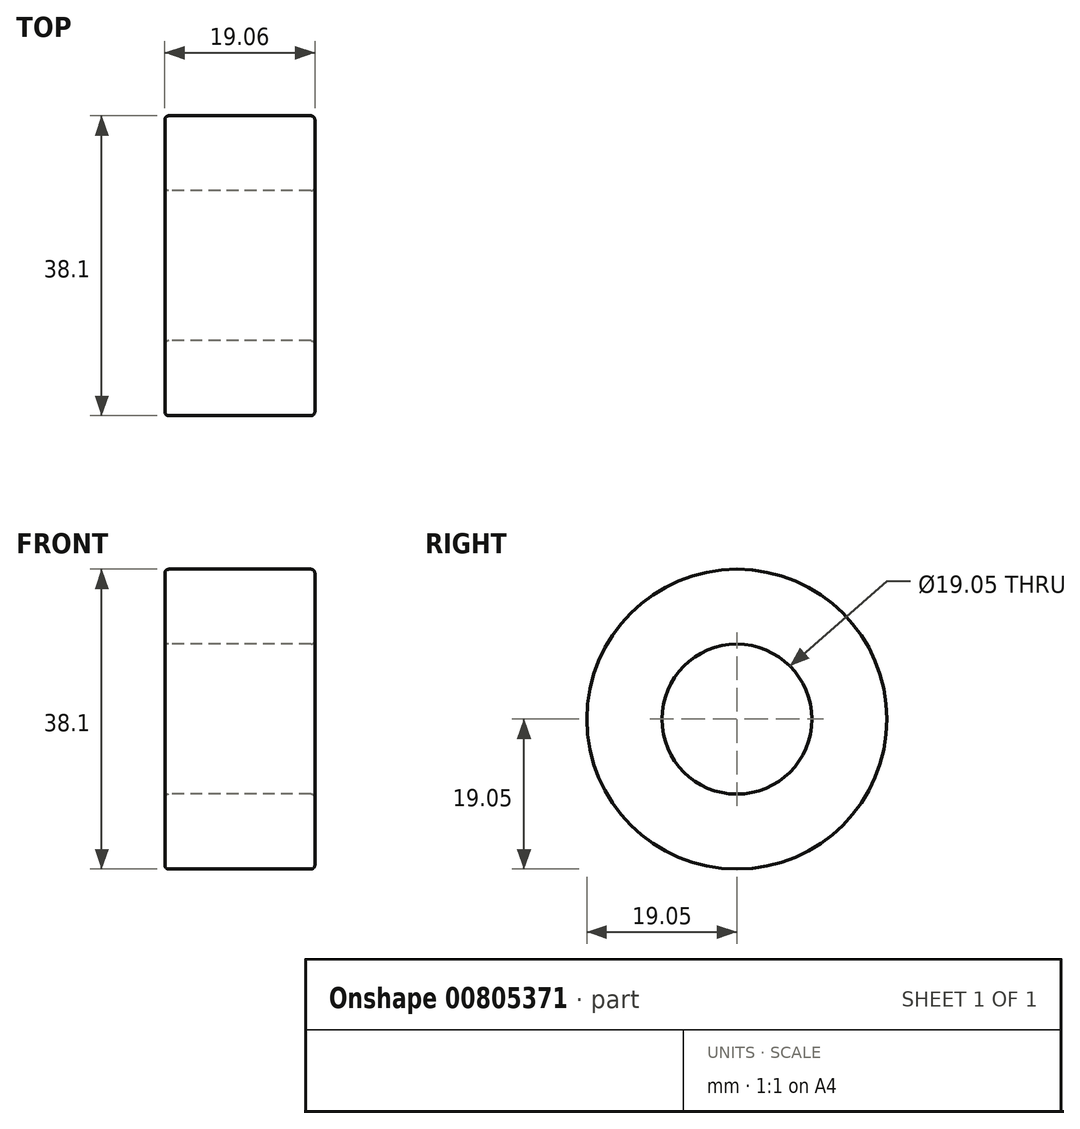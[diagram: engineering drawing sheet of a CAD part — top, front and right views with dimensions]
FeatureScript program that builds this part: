
annotation { "Feature Type Name" : "Feature", "Feature Type Description" : "" }
export const myFeature = defineFeature(function(context is Context, id is Id, definition is map)
    precondition{}
    {
        {
            var Q0;
            Q0=qCreatedBy(makeId("Right.planeOp"),FACE);
            var sketch = newSketch(context, id + "F0", { "sketchPlane" : qUnion([Q0])});
            skCircle(sketch, "E0", {"center": v(0, 0) * mm, "radius": 9.53 * mm});
            skCircle(sketch, "E1", {"center": v(0, 0) * mm, "radius": 19.05 * mm});
            skSolve(sketch);
        }
        {
            var Q0;
            Q0 = qSketchRegion(id + "F0", true);
            extrude(context, id + "F1", {"entities" : qUnion([Q0]), "endBound" : BoundingType.SYMMETRIC, "depth" : 19.05 * mm, "offsetDistance" : 25 * mm});
        }
        {
            var Q0;
            Q0=makeQuery(id+"F1.opExtrude","CAP_FACE",FACE,{"disambiguationData":[OSD([sQuery(id+"F0.wireOp",EDGE,"E0"),sQuery(id+"F0.wireOp",EDGE,"E1")])],"isStart":false});
            var Q1;
            Q1=makeQuery(id+"F1.opExtrude","CAP_FACE",FACE,{"disambiguationData":[OSD([sQuery(id+"F0.wireOp",EDGE,"E0"),sQuery(id+"F0.wireOp",EDGE,"E1")])],"isStart":true});
            fillet(context, id + "F2", {"entities" : qUnion([Q0, Q1]), "radius" : .5 * mm, "tangentPropagation" : true, "allowEdgeOverflow" : false});
        }
    });
